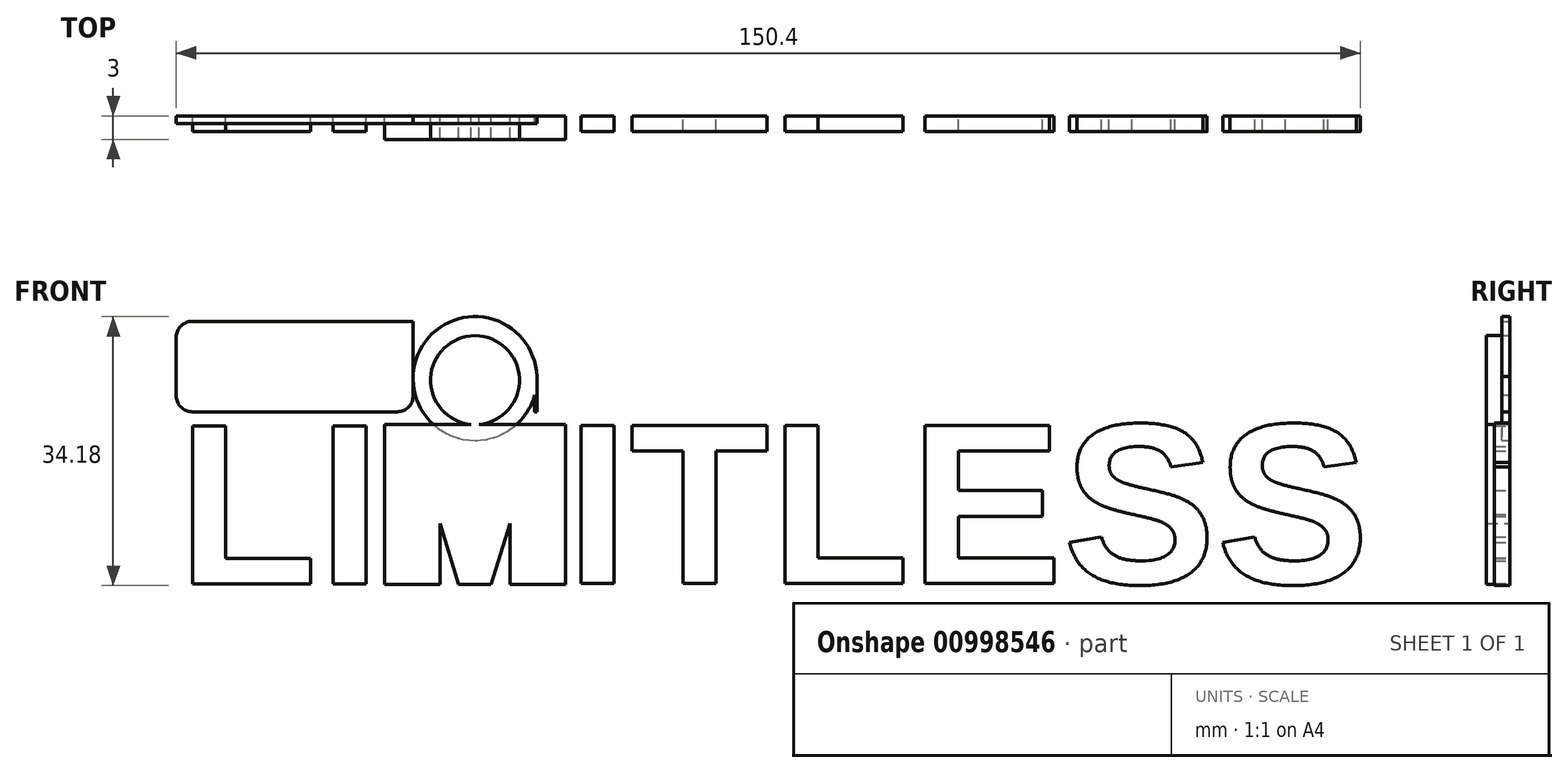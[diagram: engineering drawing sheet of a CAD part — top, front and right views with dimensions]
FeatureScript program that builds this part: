
annotation { "Feature Type Name" : "Feature", "Feature Type Description" : "" }
export const myFeature = defineFeature(function(context is Context, id is Id, definition is map)
    precondition{}
    {
        {
            var Q0;
            Q0=qCreatedBy(makeId("Front.planeOp"),FACE);
            var sketch = newSketch(context, id + "F0", { "sketchPlane" : qUnion([Q0])});
            skCircle(sketch, "E0", {"center": v(0, 25.96) * mm, "radius": 5.65 * mm});
            skLineSegment(sketch, "E1.bottom", {"start": v(-11.49, 20.33) * mm, "end": v(11.49, 20.33) * mm});
            skLineSegment(sketch, "E1.top", {"start": v(-11.49, -93.39) * mm, "end": v(11.49, -93.39) * mm});
            skLineSegment(sketch, "E2", {"start": v(-4.42, 7.8) * mm, "end": v(-2.07, 0) * mm});
            skPoint(sketch, "E3.endSnap0", {"position": v(0, -93.39) * mm});
            skLineSegment(sketch, "E4.MirrorCS", {"start": v(4.42, 7.8) * mm, "end": v(2.07, 0) * mm});
            skLineSegment(sketch, "E5", {"start": v(-4.42, -74.33) * mm, "end": v(4.42, -74.33) * mm});
            skLineSegment(sketch, "E6", {"start": v(-2.07, -68.69) * mm, "end": v(2.07, -68.69) * mm});
            skLineSegment(sketch, "E7", {"start": v(-11.49, 0) * mm, "end": v(-4.42, 0) * mm});
            skLineSegment(sketch, "E8", {"start": v(-2.07, 0) * mm, "end": v(2.07, 0) * mm});
            skLineSegment(sketch, "E9", {"start": v(4.42, 0.05) * mm, "end": v(11.49, 0.05) * mm});
            skLineSegment(sketch, "E10", {"start": v(-11.49, 0) * mm, "end": v(-11.49, 20.33) * mm});
            skLineSegment(sketch, "E11", {"start": v(11.49, 20.33) * mm, "end": v(-11.49, 20.33) * mm});
            skLineSegment(sketch, "E12", {"start": v(11.49, 20.33) * mm, "end": v(11.49, 0.05) * mm});
            skLineSegment(sketch, "E13", {"start": v(4.42, 7.8) * mm, "end": v(4.42, 0.05) * mm});
            skLineSegment(sketch, "E14", {"start": v(-2.07, 0) * mm, "end": v(-4.42, 7.8) * mm});
            skLineSegment(sketch, "E15", {"start": v(-4.42, 0) * mm, "end": v(-4.42, 7.8) * mm});
            skSolve(sketch);
        }
        {
            var Q0;
            Q0=qSketchRegion(id+"F0",true);
            extrude(context, id + "F1", {"entities" : qUnion([Q0]), "depth" : 3 * mm, "offsetDistance" : 25 * mm});
        }
        {
            var Q0;
            Q0=qCreatedBy(makeId("Front.planeOp"),FACE);
            var sketch = newSketch(context, id + "F2", { "sketchPlane" : qUnion([Q0])});
            skText(sketch, "E16", { "text": "ITLESS", "fontName": "Arimo-Bold.ttf"});
            const initialGuessF2  = {"E16": [0.0115, 0.00015, 1, 0, 0.021]};
            skSetInitialGuess(sketch, initialGuessF2);
            skSolve(sketch);
        }
        {
            var Q0;
            Q0=qCreatedBy(makeId("Front.planeOp"),FACE);
            var sketch = newSketch(context, id + "F3", { "sketchPlane" : qUnion([Q0])});
            skText(sketch, "E17", { "text": "LI", "fontName": "Arimo-Bold.ttf"});
            const initialGuessF3  = {"E17": [-0.0378, 6e-05, 1, 0, 0.021]};
            skSetInitialGuess(sketch, initialGuessF3);
            skSolve(sketch);
        }
        {
            var Q0;
            Q0 = qSketchRegion(id + "F2", true);
            extrude(context, id + "F4", {"entities" : qUnion([Q0]), "operationType" : NewBodyOperationType.ADD, "depth" : 2 * mm, "offsetDistance" : 25 * mm});
        }
        {
            var Q0;
            Q0 = qSketchRegion(id + "F3", true);
            extrude(context, id + "F5", {"entities" : qUnion([Q0]), "depth" : 2 * mm, "offsetDistance" : 25 * mm});
        }
        {
            var Q0;
            Q0=qCreatedBy(makeId("Front.planeOp"),FACE);
            var sketch = newSketch(context, id + "F6", { "sketchPlane" : qUnion([Q0])});
            skLineSegment(sketch, "E18.bottom", {"start": v(-37.94, -1.8) * mm, "end": v(113.54, -1.8) * mm});
            skLineSegment(sketch, "E18.top", {"start": v(-37.94, 33.43) * mm, "end": v(113.54, 33.43) * mm});
            skLineSegment(sketch, "E18.left", {"start": v(-37.94, -1.8) * mm, "end": v(-37.94, 33.43) * mm});
            skLineSegment(sketch, "E18.right", {"start": v(113.54, -1.8) * mm, "end": v(113.54, 33.43) * mm});
            skLineSegment(sketch, "E19.bottom", {"start": v(-37.94, 33.43) * mm, "end": v(-7.87, 33.43) * mm});
            skLineSegment(sketch, "E19.top", {"start": v(-37.94, 21.95) * mm, "end": v(-7.87, 21.95) * mm});
            skLineSegment(sketch, "E19.left", {"start": v(-37.94, 33.43) * mm, "end": v(-37.94, 21.95) * mm});
            skLineSegment(sketch, "E19.right", {"start": v(-7.87, 33.43) * mm, "end": v(-7.87, 21.95) * mm});
            skLineSegment(sketch, "E20.bottom", {"start": v(113.54, 33.43) * mm, "end": v(7.58, 33.43) * mm});
            skLineSegment(sketch, "E20.top", {"start": v(113.54, 21.95) * mm, "end": v(7.58, 21.95) * mm});
            skLineSegment(sketch, "E20.left", {"start": v(113.54, 33.43) * mm, "end": v(113.54, 21.95) * mm});
            skLineSegment(sketch, "E20.right", {"start": v(7.58, 33.43) * mm, "end": v(7.58, 21.95) * mm});
            skCircle(sketch, "E21", {"center": v(0, 26.17) * mm, "radius": 7.87 * mm});
            skLineSegment(sketch, "E22.bottom", {"start": v(-29.5, 21.95) * mm, "end": v(-20.92, 21.95) * mm});
            skLineSegment(sketch, "E22.top", {"start": v(-29.5, 5.46) * mm, "end": v(-20.92, 5.46) * mm});
            skLineSegment(sketch, "E22.left", {"start": v(-29.5, 21.95) * mm, "end": v(-29.5, 5.46) * mm});
            skLineSegment(sketch, "E22.right", {"start": v(-20.92, 21.95) * mm, "end": v(-20.92, 5.46) * mm});
            skLineSegment(sketch, "E23.bottom", {"start": v(45.58, 21.95) * mm, "end": v(54.16, 21.95) * mm});
            skLineSegment(sketch, "E23.top", {"start": v(45.58, 5.59) * mm, "end": v(54.16, 5.59) * mm});
            skLineSegment(sketch, "E23.left", {"start": v(45.58, 21.95) * mm, "end": v(45.58, 5.59) * mm});
            skLineSegment(sketch, "E23.right", {"start": v(54.16, 21.95) * mm, "end": v(54.16, 5.59) * mm});
            skLineSegment(sketch, "E24.bottom", {"start": v(19.46, -1.8) * mm, "end": v(23.94, -1.8) * mm});
            skLineSegment(sketch, "E24.top", {"start": v(19.46, 14.96) * mm, "end": v(23.94, 14.96) * mm});
            skLineSegment(sketch, "E24.left", {"start": v(19.46, -1.8) * mm, "end": v(19.46, 14.96) * mm});
            skLineSegment(sketch, "E24.right", {"start": v(23.94, -1.8) * mm, "end": v(23.94, 14.96) * mm});
            skLineSegment(sketch, "E25.bottom", {"start": v(32.78, -1.8) * mm, "end": v(36.87, -1.8) * mm});
            skLineSegment(sketch, "E25.top", {"start": v(32.78, 15.09) * mm, "end": v(36.87, 15.09) * mm});
            skLineSegment(sketch, "E25.left", {"start": v(32.78, -1.8) * mm, "end": v(32.78, 15.09) * mm});
            skLineSegment(sketch, "E25.right", {"start": v(36.87, -1.8) * mm, "end": v(36.87, 15.09) * mm});
            skLineSegment(sketch, "E26", {"start": v(7.86, 26.44) * mm, "end": v(7.86, 21.95) * mm});
            skLineSegment(sketch, "E27", {"start": v(7.86, 26.44) * mm, "end": v(7.86, 33.43) * mm});
            skSolve(sketch);
        }
        {
            var Q0;
            {var subQ17=sQuery(id+"F6.wireOp",EDGE,"E18.left");Q0=makeQuery(id+"F6.imprint","IMPRINT",FACE,{"disambiguationData":[TD([[makeQuery(id+"F6.imprint","IMPRINT",EDGE,{"derivedFrom":subQ17}),-1.0]])]});}
            var Q1;
            {var subQ0=sQuery(id+"F6.wireOp",EDGE,"E21");var subQ1=sQuery(id+"F6.wireOp",EDGE,"E18.top");var subQ2=makeQuery(id+"F6.imprint","INTERSECT",VERTEX,{"disambiguationData":[OD(0.0)],"derivedFrom":[subQ1,subQ0]});Q1=makeQuery(id+"F6.imprint","IMPRINT",FACE,{"disambiguationData":[TD([[makeQuery(id+"F6.imprint","IMPRINT",EDGE,{"disambiguationData":[TD([[subQ2,-1.0]])],"derivedFrom":subQ1}),-1.0]])]});}
            var Q2;
            {var subQ0=sQuery(id+"F6.wireOp",EDGE,"E21");var subQ1=sQuery(id+"F6.wireOp",EDGE,"E18.top");var subQ2=makeQuery(id+"F6.imprint","INTERSECT",VERTEX,{"disambiguationData":[OD(0.0)],"derivedFrom":[subQ1,subQ0]});Q2=makeQuery(id+"F6.imprint","IMPRINT",FACE,{"disambiguationData":[TD([[makeQuery(id+"F6.imprint","IMPRINT",EDGE,{"disambiguationData":[TD([[subQ2,-1.0]])],"derivedFrom":subQ1}),1.0]])]});}
            var Q3;
            {var subQ0=sQuery(id+"F6.wireOp",EDGE,"E21");var subQ1=sQuery(id+"F6.wireOp",EDGE,"E20.right");var subQ2=makeQuery(id+"F6.imprint","INTERSECT",VERTEX,{"disambiguationData":[OD(0.0)],"derivedFrom":[subQ1,subQ0]});Q3=makeQuery(id+"F6.imprint","IMPRINT",FACE,{"disambiguationData":[TD([[makeQuery(id+"F6.imprint","IMPRINT",EDGE,{"disambiguationData":[TD([[subQ2,-1.0]])],"derivedFrom":subQ1}),1.0]])]});}
            var Q4;
            {var subQ0=sQuery(id+"F6.wireOp",EDGE,"E20.right");var subQ1=sQuery(id+"F6.wireOp",EDGE,"E20.top");var subQ2=makeQuery(id+"F6.imprint","INTERSECT",VERTEX,{"derivedFrom":[subQ1,subQ0]});Q4=makeQuery(id+"F6.imprint","IMPRINT",FACE,{"disambiguationData":[TD([[makeQuery(id+"F6.imprint","IMPRINT",EDGE,{"disambiguationData":[TD([[subQ2,1.0]])],"derivedFrom":subQ1}),-1.0]])]});}
            extrude(context, id + "F7", {"entities" : qUnion([Q0, Q1, Q2, Q3, Q4]), "depth" : 1 * mm, "offsetDistance" : 25 * mm});
        }
        {
            var Q0;
            Q0=makeQuery(id+"F7.opExtrude","SWEPT_EDGE",EDGE,{"disambiguationData":[OSD([sQuery(id+"F6.wireOp",EDGE,"E18.left"),sQuery(id+"F6.wireOp",EDGE,"E19.top"),sQuery(id+"F6.wireOp",EDGE,"E19.left")])]});
            var Q1;
            Q1=makeQuery(id+"F7.opExtrude","SWEPT_EDGE",EDGE,{"disambiguationData":[OSD([sQuery(id+"F6.wireOp",EDGE,"E19.top"),sQuery(id+"F6.wireOp",EDGE,"E22.bottom"),sQuery(id+"F6.wireOp",EDGE,"E22.right")])]});
            var Q2;
            Q2=makeQuery(id+"F7.opExtrude","SWEPT_EDGE",EDGE,{"disambiguationData":[OSD([sQuery(id+"F6.wireOp",EDGE,"E18.bottom"),sQuery(id+"F6.wireOp",EDGE,"E18.left")])]});
            var Q3;
            Q3=makeQuery(id+"F7.opExtrude","SWEPT_EDGE",EDGE,{"disambiguationData":[OSD([sQuery(id+"F6.wireOp",EDGE,"E22.top"),sQuery(id+"F6.wireOp",EDGE,"E22.right")])]});
            var Q4;
            Q4=makeQuery(id+"F7.opExtrude","SWEPT_EDGE",EDGE,{"disambiguationData":[OSD([sQuery(id+"F6.wireOp",EDGE,"E19.top"),sQuery(id+"F6.wireOp",EDGE,"E22.bottom"),sQuery(id+"F6.wireOp",EDGE,"E22.left")])]});
            var Q5;
            Q5=makeQuery(id+"F7.opExtrude","SWEPT_EDGE",EDGE,{"disambiguationData":[OSD([sQuery(id+"F6.wireOp",EDGE,"E22.top"),sQuery(id+"F6.wireOp",EDGE,"E22.left")])]});
            var Q6;
            Q6=makeQuery(id+"F7.opExtrude","SWEPT_EDGE",EDGE,{"disambiguationData":[OSD([sQuery(id+"F6.wireOp",EDGE,"E19.top"),sQuery(id+"F6.wireOp",EDGE,"E19.right")])]});
            var Q7;
            Q7=makeQuery(id+"F7.opExtrude","SWEPT_EDGE",EDGE,{"disambiguationData":[OSD([sQuery(id+"F6.wireOp",EDGE,"E20.top"),sQuery(id+"F6.wireOp",EDGE,"E26")])]});
            var Q8;
            Q8=makeQuery(id+"F7.opExtrude","SWEPT_EDGE",EDGE,{"disambiguationData":[OSD([sQuery(id+"F6.wireOp",EDGE,"E20.top"),sQuery(id+"F6.wireOp",EDGE,"E23.bottom"),sQuery(id+"F6.wireOp",EDGE,"E23.left")])]});
            var Q9;
            Q9=makeQuery(id+"F7.opExtrude","SWEPT_EDGE",EDGE,{"disambiguationData":[OSD([sQuery(id+"F6.wireOp",EDGE,"E18.right"),sQuery(id+"F6.wireOp",EDGE,"E20.top"),sQuery(id+"F6.wireOp",EDGE,"E20.left")])]});
            var Q10;
            Q10=makeQuery(id+"F7.opExtrude","SWEPT_EDGE",EDGE,{"disambiguationData":[OSD([sQuery(id+"F6.wireOp",EDGE,"E18.bottom"),sQuery(id+"F6.wireOp",EDGE,"E24.bottom"),sQuery(id+"F6.wireOp",EDGE,"E24.left")])]});
            var Q11;
            Q11=makeQuery(id+"F7.opExtrude","SWEPT_EDGE",EDGE,{"disambiguationData":[OSD([sQuery(id+"F6.wireOp",EDGE,"E18.bottom"),sQuery(id+"F6.wireOp",EDGE,"E25.bottom"),sQuery(id+"F6.wireOp",EDGE,"E25.left")])]});
            var Q12;
            Q12=makeQuery(id+"F7.opExtrude","SWEPT_EDGE",EDGE,{"disambiguationData":[OSD([sQuery(id+"F6.wireOp",EDGE,"E24.top"),sQuery(id+"F6.wireOp",EDGE,"E24.left")])]});
            var Q13;
            Q13=makeQuery(id+"F7.opExtrude","SWEPT_EDGE",EDGE,{"disambiguationData":[OSD([sQuery(id+"F6.wireOp",EDGE,"E25.top"),sQuery(id+"F6.wireOp",EDGE,"E25.left")])]});
            var Q14;
            Q14=makeQuery(id+"F7.opExtrude","SWEPT_EDGE",EDGE,{"disambiguationData":[OSD([sQuery(id+"F6.wireOp",EDGE,"E18.bottom"),sQuery(id+"F6.wireOp",EDGE,"E25.bottom"),sQuery(id+"F6.wireOp",EDGE,"E25.right")])]});
            var Q15;
            Q15=makeQuery(id+"F7.opExtrude","SWEPT_EDGE",EDGE,{"disambiguationData":[OSD([sQuery(id+"F6.wireOp",EDGE,"E25.top"),sQuery(id+"F6.wireOp",EDGE,"E25.right")])]});
            var Q16;
            Q16=makeQuery(id+"F7.opExtrude","SWEPT_EDGE",EDGE,{"disambiguationData":[OSD([sQuery(id+"F6.wireOp",EDGE,"E18.bottom"),sQuery(id+"F6.wireOp",EDGE,"E24.bottom"),sQuery(id+"F6.wireOp",EDGE,"E24.right")])]});
            var Q17;
            Q17=makeQuery(id+"F7.opExtrude","SWEPT_EDGE",EDGE,{"disambiguationData":[OSD([sQuery(id+"F6.wireOp",EDGE,"E24.top"),sQuery(id+"F6.wireOp",EDGE,"E24.right")])]});
            var Q18;
            Q18=makeQuery(id+"F7.opExtrude","SWEPT_EDGE",EDGE,{"disambiguationData":[OSD([sQuery(id+"F6.wireOp",EDGE,"E20.top"),sQuery(id+"F6.wireOp",EDGE,"E23.bottom"),sQuery(id+"F6.wireOp",EDGE,"E23.right")])]});
            var Q19;
            Q19=makeQuery(id+"F7.opExtrude","SWEPT_EDGE",EDGE,{"disambiguationData":[OSD([sQuery(id+"F6.wireOp",EDGE,"E23.top"),sQuery(id+"F6.wireOp",EDGE,"E23.right")])]});
            var Q20;
            Q20=makeQuery(id+"F7.opExtrude","SWEPT_EDGE",EDGE,{"disambiguationData":[OSD([sQuery(id+"F6.wireOp",EDGE,"E23.top"),sQuery(id+"F6.wireOp",EDGE,"E23.left")])]});
            var Q21;
            Q21=makeQuery(id+"F7.opExtrude","SWEPT_EDGE",EDGE,{"disambiguationData":[OSD([sQuery(id+"F6.wireOp",EDGE,"E18.bottom"),sQuery(id+"F6.wireOp",EDGE,"E18.right")])]});
            fillet(context, id + "F8", {"entities" : qUnion([Q0, Q1, Q2, Q3, Q4, Q5, Q6, Q7, Q8, Q9, Q10, Q11, Q12, Q13, Q14, Q15, Q16, Q17, Q18, Q19, Q20, Q21]), "radius" : 2 * mm, "tangentPropagation" : true, "allowEdgeOverflow" : false});
        }
    });
